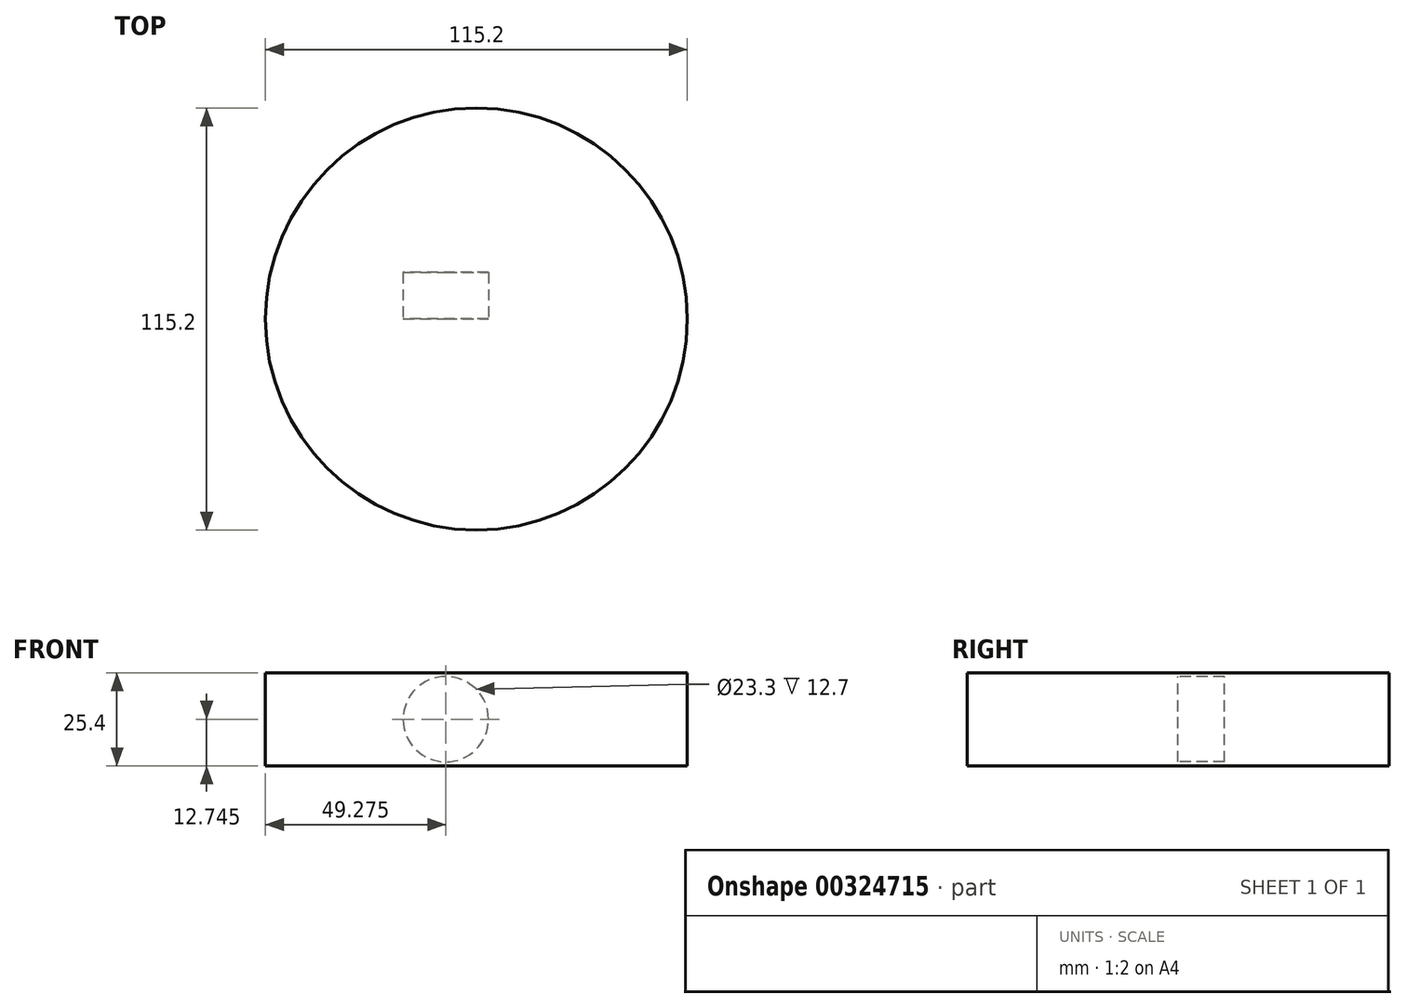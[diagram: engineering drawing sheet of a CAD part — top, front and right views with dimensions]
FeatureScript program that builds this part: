
annotation { "Feature Type Name" : "Feature", "Feature Type Description" : "" }
export const myFeature = defineFeature(function(context is Context, id is Id, definition is map)
    precondition{}
    {
        {
            var Q0;
            Q0=qCreatedBy(makeId("Top.planeOp"),FACE);
            var sketch = newSketch(context, id + "F0", { "sketchPlane" : qUnion([Q0])});
            skCircle(sketch, "E0", {"center": v(0, 0) * mm, "radius": 57.6 * mm});
            skSolve(sketch);
        }
        {
            var Q0;
            Q0=qSketchRegion(id+"F0",true);
            extrude(context, id + "F1", {"entities" : qUnion([Q0]), "depth" : 25.4 * mm});
        }
        {
            var Q0;
            Q0=qCreatedBy(makeId("Top.planeOp"),FACE);
            var sketch = newSketch(context, id + "F2", { "sketchPlane" : qUnion([Q0])});
            skCircle(sketch, "E1", {"center": v(0, 0) * mm, "radius": 41.9 * mm});
            skSolve(sketch);
        }
        {
            var Q0;
            Q0=qSketchRegion(id+"F2",true);
            extrude(context, id + "F3", {"entities" : qUnion([Q0]), "operationType" : NewBodyOperationType.REMOVE, "endBound" : BoundingType.THROUGH_ALL, "oppositeDirection" : true, "depth" : 25.4 * mm});
        }
        {
            var Q0;
            Q0=qCreatedBy(makeId("Front.planeOp"),FACE);
            var sketch = newSketch(context, id + "F4", { "sketchPlane" : qUnion([Q0])});
            skCircle(sketch, "E2", {"center": v(-8.32, 12.75) * mm, "radius": 11.65 * mm});
            skPoint(sketch, "E2.first.point", {"position": v(-15.82, 21.67) * mm});
            skPoint(sketch, "E2.second.point", {"position": v(0, 4.6) * mm});
            skPoint(sketch, "E2.third.point", {"position": v(-19.87, 14.27) * mm});
            skSolve(sketch);
        }
        {
            var Q0;
            Q0=qSketchRegion(id+"F4",true);
            extrude(context, id + "F5", {"entities" : qUnion([Q0]), "operationType" : NewBodyOperationType.REMOVE, "oppositeDirection" : true, "depth" : 12.7 * mm});
        }
    });
